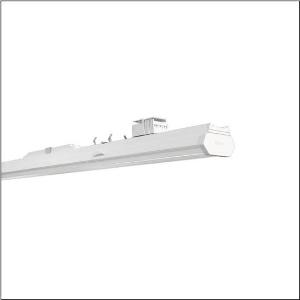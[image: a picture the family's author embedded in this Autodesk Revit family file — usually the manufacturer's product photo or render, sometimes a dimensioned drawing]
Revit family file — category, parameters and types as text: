
# Revit family: licross_r__21_protected_mo_52td12dn4a5g3s_ad63
name_source: partatom
category: Lighting Fixtures
units: mm (PartAtom-declared; Revit-internal decimal feet)

## family parameters
Cut with Voids When Loaded = No
Host = Face
Light Source = No
Part Type = Normal
Room Calculation Point = No
Round Connector Dimension = Use Diameter
Shared = No

## types (1)
- --- (1 x LED, 940 lm, 6.8 W, 4000K)
    Apparent Load = 7 VA
    CIE Flux Codes = 73 92 98 99 100
    Color Rendering = 80
    Color Temperature = 4000K
    Default Elevation = 1800 mm
    Description = Licross® 21 Protected MO, luminaire insert, of sheet steel, galvanised, coil coated, white, length: 1.500mm, width: 90mm, height: 103mm, LED rated luminous flux: 10.700lm, light colour: 840, control gear: DALI 2, with plug, 6-pole, with phase selection, for trunking rail, 14-core, mains connection: 220..240V, AC, 50/60Hz, rated input power: 66W, for trunking rail, 14-core, halogen-free wiring, for emergency light function, converter,control gear: single battery element, battery: LiFeP04, 9Ah, primary light control with lens, of plastic, primary optical cover: cover, of PMMA, light emission: direct distribution, primary light characteristic: symmetric, protection rating (complete): IP54, insulation class (complete): insulation class I (protective earthing), certification: CE, UKCA, protection symbol: D if used in an environment with non-conductive dust loads with corresponding accessories, impact resistance: IK06, permissible ambient temperature for indoor applications: +5..+35°C, standard: EN 60598-2-22, LABS conformity tested according to VDMA 24364:2018-05, reducing of maximum allowable ambient temperature of 5°C with ceiling mounting, corresponds to IFS (International Featured Standards) requirements for safety and quality in the food industry, packaging unit: 1 piece
    Height = 92 mm
    Lamp = 1 x LED
    Lamp Light Flux = 940 lm
    Lamp Power = 6.8 W
    Lamp count = 1
    Length = 1500 mm
    Luminous efficacy = 138 lm/W
    Manufacturer = Siteco
    ModVariant = No
    Model = 52TD12DN4A5G3S
    Mounting Place = Ceiling
    Mounting Type = Pendant
    Number of Poles = 1
    OnlyDefault = Yes
    Power Factor = 1
    Product Name = Licross® 21 Protected MO
    Product group = luminaire insert
    ProductGroupID = 901
    Protection Class = Protection class I
    Protection Degree = IP 54
    RLX_Detail_Level = 1
    RLX_Emergency_Light_Flux = 0 lm
    RLX_Emergency_Type = 0
    RLX_Emergency_Type_DB = No
    RlxData = <blob elided: 24821 chars, md5=4d0ff6af>
    Socket = socket
    Standby Power = 0 W
    System Light Flux = 940 lm
    System Power = 7 W
    Type Comments = : emergency light operation: 3 h
    Type Image = l_1256148.jpg
    URL = http://relux.com
    VarID = @adj_041019
    Voltage = 0 V
    Weight = 0.00 kg
    Width = 88 mm

## geometry (parser evidence)
native form markers: Blend x4, Sweep x9
no freeform markers — native parametric forms only
